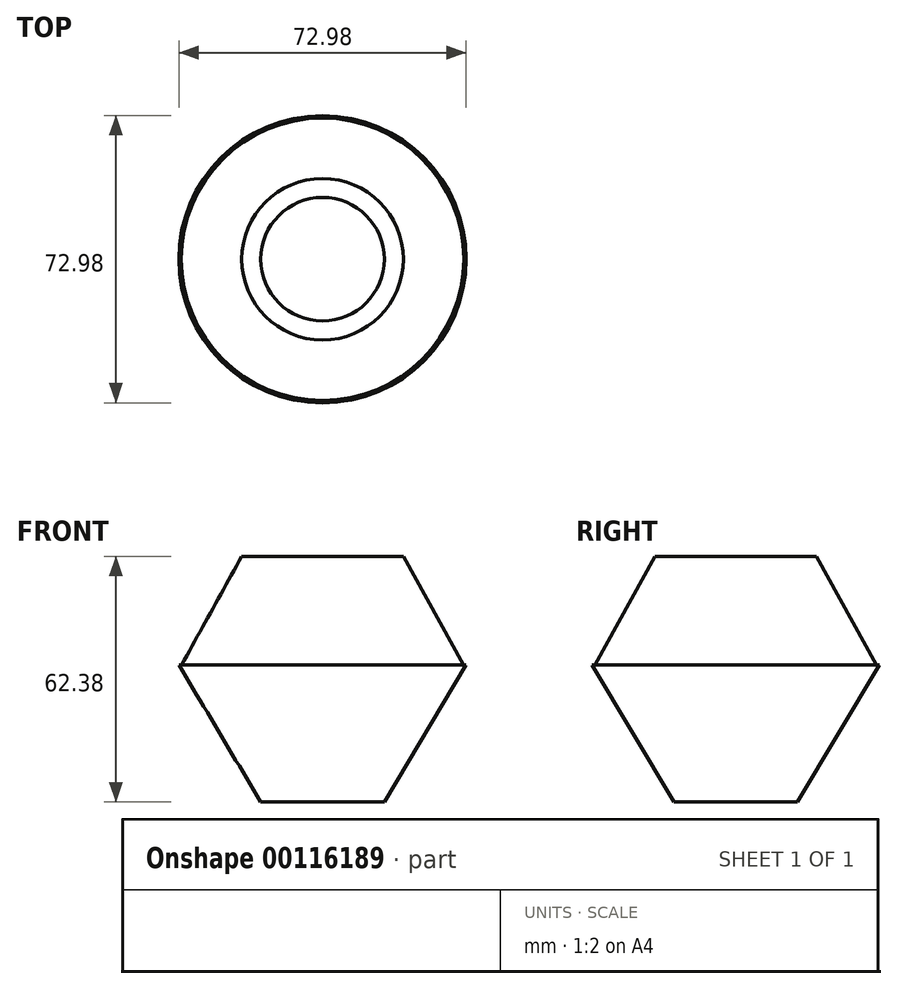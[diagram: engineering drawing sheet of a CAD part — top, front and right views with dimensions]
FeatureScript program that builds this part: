
annotation { "Feature Type Name" : "Feature", "Feature Type Description" : "" }
export const myFeature = defineFeature(function(context is Context, id is Id, definition is map)
    precondition{}
    {
        {
            var Q0;
            Q0=qCreatedBy(makeId("Front.planeOp"),FACE);
            var sketch = newSketch(context, id + "F0", { "sketchPlane" : qUnion([Q0])});
            skLineSegment(sketch, "E0", {"start": v(-28.7, 33.28) * mm, "end": v(-28.7, -31.58) * mm, "construction": true});
            skLineSegment(sketch, "E1", {"start": v(-49.22, 33.67) * mm, "end": v(-64.58, 5.94) * mm});
            skLineSegment(sketch, "E2", {"start": v(-65.19, 6.1) * mm, "end": v(-44.4, -28.7) * mm});
            skSolve(sketch);
        }
        {
            var Q0;
            Q0=sQuery(id+"F0.wireOp",EDGE,"E1");
            var Q1;
            Q1=sQuery(id+"F0.wireOp",EDGE,"E2");
            var Q2;
            Q2=sQuery(id+"F0.wireOp",EDGE,"E0");
            revolve(context, id + "F1", {"bodyType" : ToolBodyType.SURFACE, "surfaceEntities" : qUnion([Q0, Q1]), "axis" : qUnion([Q2]), "revolveType" : RevolveType.FULL});
        }
    });
